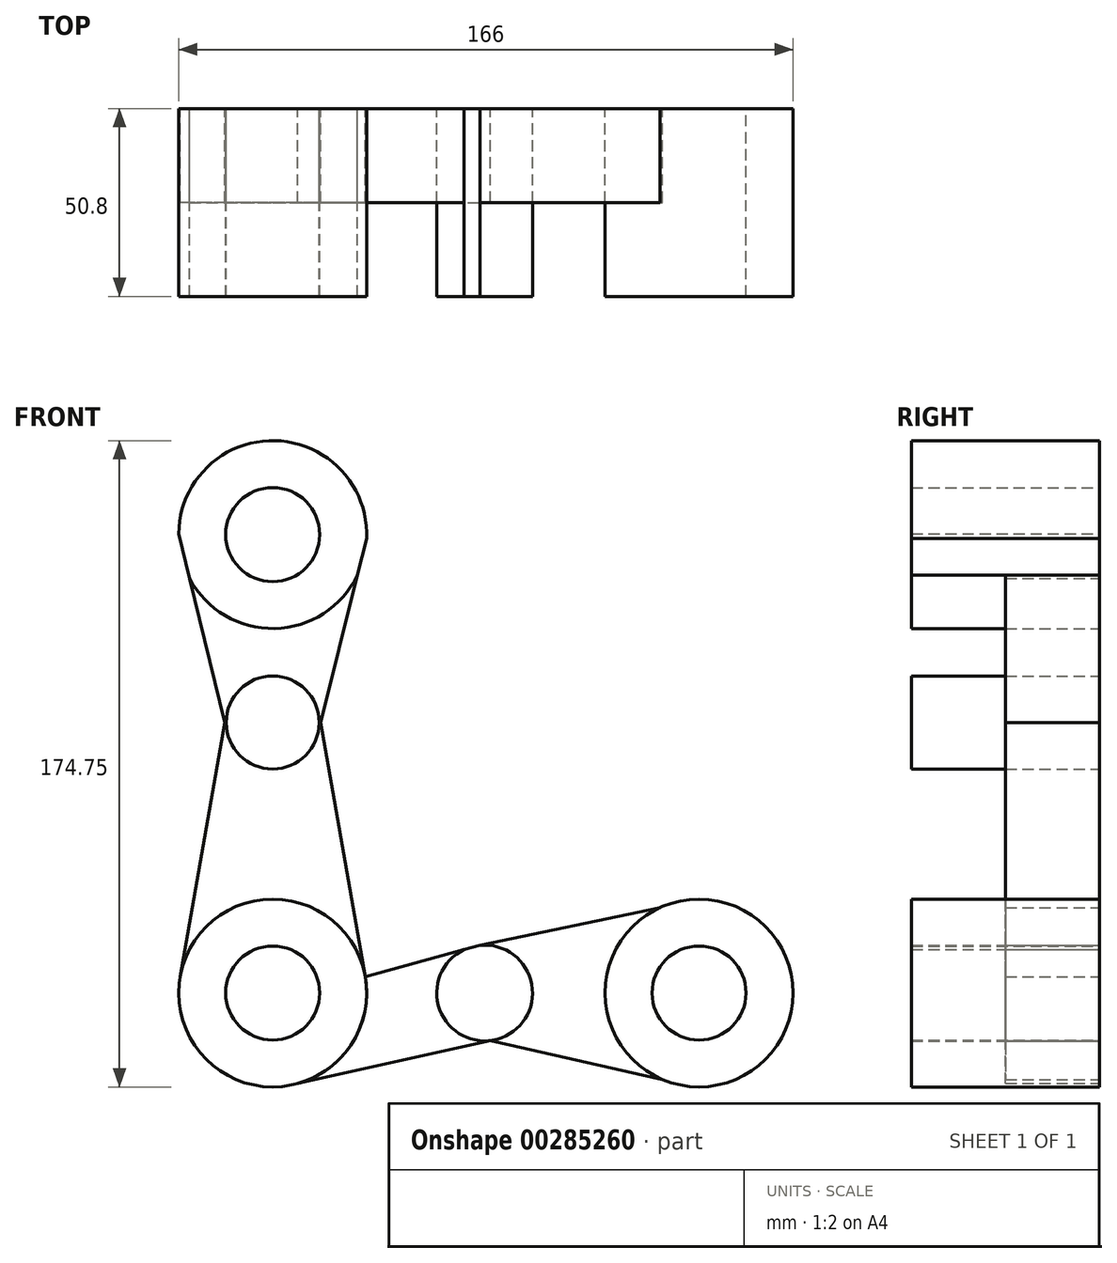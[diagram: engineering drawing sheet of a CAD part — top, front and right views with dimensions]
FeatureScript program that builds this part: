
annotation { "Feature Type Name" : "Feature", "Feature Type Description" : "" }
export const myFeature = defineFeature(function(context is Context, id is Id, definition is map)
    precondition{}
    {
        {
            var Q0;
            Q0=qCreatedBy(makeId("Front.planeOp"),FACE);
            var sketch = newSketch(context, id + "F0", { "sketchPlane" : qUnion([Q0])});
            skLineSegment(sketch, "E0", {"start": v(-57.93, -73.15) * mm, "end": v(-115.2, -73.15) * mm});
            skLineSegment(sketch, "E1", {"start": v(-57.93, -73.15) * mm, "end": v(0, -73.15) * mm});
            skLineSegment(sketch, "E2", {"start": v(-115.2, -73.15) * mm, "end": v(-115.2, 0) * mm});
            skLineSegment(sketch, "E3", {"start": v(-115.2, 0) * mm, "end": v(-115.2, 50.8) * mm});
            skCircle(sketch, "E4", {"center": v(-115.2, 50.8) * mm, "radius": 25.4 * mm});
            skCircle(sketch, "E5", {"center": v(-115.2, -73.15) * mm, "radius": 25.4 * mm});
            skCircle(sketch, "E6", {"center": v(0, -73.15) * mm, "radius": 25.4 * mm});
            skCircle(sketch, "E7", {"center": v(-115.2, 0) * mm, "radius": 12.57 * mm});
            skCircle(sketch, "E8", {"center": v(-57.93, -73.15) * mm, "radius": 12.95 * mm});
            skLineSegment(sketch, "E9", {"start": v(-140.6, 51.02) * mm, "end": v(-128.13, 0) * mm});
            skLineSegment(sketch, "E10", {"start": v(-128.13, 0) * mm, "end": v(-140.21, -68.75) * mm});
            skLineSegment(sketch, "E11", {"start": v(-89.82, 49.72) * mm, "end": v(-102.24, 0) * mm});
            skLineSegment(sketch, "E12", {"start": v(-102.24, 0) * mm, "end": v(-90.18, -68.75) * mm});
            skLineSegment(sketch, "E13", {"start": v(-90.18, -68.75) * mm, "end": v(-59.14, -60.25) * mm});
            skLineSegment(sketch, "E14", {"start": v(-59.14, -60.25) * mm, "end": v(-10.54, -50.04) * mm});
            skLineSegment(sketch, "E15", {"start": v(-56.39, -86) * mm, "end": v(-9.9, -96.54) * mm});
            skLineSegment(sketch, "E16", {"start": v(-108.46, -97.64) * mm, "end": v(-56.39, -86) * mm});
            skSolve(sketch);
        }
        {
            var Q0;
            {var subQ1=sQuery(id+"F0.wireOp",EDGE,"E4");var subQ6=makeQuery(id+"F0.imprint","INTERSECT",VERTEX,{"derivedFrom":[sQuery(id+"F0.wireOp",EDGE,"E3"),subQ1]});Q0=makeQuery(id+"F0.imprint","IMPRINT",FACE,{"disambiguationData":[TD([[makeQuery(id+"F0.imprint","IMPRINT",EDGE,{"disambiguationData":[TD([[subQ6,1.0]])],"derivedFrom":subQ1}),1.0]])]});}
            var Q1;
            {var subQ0=sQuery(id+"F0.wireOp",EDGE,"E3");var subQ1=sQuery(id+"F0.wireOp",EDGE,"E2");var subQ2=makeQuery(id+"F0.imprint","INTERSECT",VERTEX,{"derivedFrom":[subQ1,subQ0]});Q1=makeQuery(id+"F0.imprint","IMPRINT",FACE,{"disambiguationData":[TD([[makeQuery(id+"F0.imprint","IMPRINT",EDGE,{"disambiguationData":[TD([[subQ2,1.0]])],"derivedFrom":subQ1}),1.0]])]});}
            var Q2;
            {var subQ0=sQuery(id+"F0.wireOp",EDGE,"E3");var subQ1=sQuery(id+"F0.wireOp",EDGE,"E2");var subQ2=makeQuery(id+"F0.imprint","INTERSECT",VERTEX,{"derivedFrom":[subQ1,subQ0]});Q2=makeQuery(id+"F0.imprint","IMPRINT",FACE,{"disambiguationData":[TD([[makeQuery(id+"F0.imprint","IMPRINT",EDGE,{"disambiguationData":[TD([[subQ2,1.0]])],"derivedFrom":subQ1}),-1.0]])]});}
            var Q3;
            {var subQ3=sQuery(id+"F0.wireOp",EDGE,"E2");var subQ4=sQuery(id+"F0.wireOp",EDGE,"E0");var subQ5=makeQuery(id+"F0.imprint","INTERSECT",VERTEX,{"derivedFrom":[subQ4,subQ3]});Q3=makeQuery(id+"F0.imprint","IMPRINT",FACE,{"disambiguationData":[TD([[makeQuery(id+"F0.imprint","IMPRINT",EDGE,{"disambiguationData":[TD([[subQ5,1.0]])],"derivedFrom":subQ4}),1.0]])]});}
            var Q4;
            {var subQ0=sQuery(id+"F0.wireOp",EDGE,"E2");var subQ1=sQuery(id+"F0.wireOp",EDGE,"E0");var subQ2=makeQuery(id+"F0.imprint","INTERSECT",VERTEX,{"derivedFrom":[subQ1,subQ0]});Q4=makeQuery(id+"F0.imprint","IMPRINT",FACE,{"disambiguationData":[TD([[makeQuery(id+"F0.imprint","IMPRINT",EDGE,{"disambiguationData":[TD([[subQ2,1.0]])],"derivedFrom":subQ1}),-1.0]])]});}
            var Q5;
            {var subQ3=sQuery(id+"F0.wireOp",EDGE,"E0");var subQ5=sQuery(id+"F0.wireOp",EDGE,"E1");var subQ6=makeQuery(id+"F0.imprint","INTERSECT",VERTEX,{"derivedFrom":[subQ3,subQ5]});Q5=makeQuery(id+"F0.imprint","IMPRINT",FACE,{"disambiguationData":[TD([[makeQuery(id+"F0.imprint","IMPRINT",EDGE,{"disambiguationData":[TD([[subQ6,-1.0]])],"derivedFrom":subQ3}),-1.0]])]});}
            var Q6;
            {var subQ0=sQuery(id+"F0.wireOp",EDGE,"E1");var subQ1=sQuery(id+"F0.wireOp",EDGE,"E0");var subQ2=makeQuery(id+"F0.imprint","INTERSECT",VERTEX,{"derivedFrom":[subQ1,subQ0]});Q6=makeQuery(id+"F0.imprint","IMPRINT",FACE,{"disambiguationData":[TD([[makeQuery(id+"F0.imprint","IMPRINT",EDGE,{"disambiguationData":[TD([[subQ2,-1.0]])],"derivedFrom":subQ1}),1.0]])]});}
            var Q7;
            {var subQ0=sQuery(id+"F0.wireOp",EDGE,"E6");var subQ1=makeQuery(id+"F0.imprint","INTERSECT",VERTEX,{"derivedFrom":[subQ0,sQuery(id+"F0.wireOp",EDGE,"E14")]});Q7=makeQuery(id+"F0.imprint","IMPRINT",FACE,{"disambiguationData":[TD([[makeQuery(id+"F0.imprint","IMPRINT",EDGE,{"disambiguationData":[TD([[subQ1,-1.0]])],"derivedFrom":subQ0}),1.0]])]});}
            extrude(context, id + "F1", {"entities" : qUnion([Q0, Q1, Q2, Q3, Q4, Q5, Q6, Q7]), "depth" : 50.8 * mm});
        }
        {
            var Q0;
            {var subQ0=sQuery(id+"F0.wireOp",EDGE,"E10");Q0=makeQuery(id+"F0.imprint","IMPRINT",FACE,{"disambiguationData":[TD([[makeQuery(id+"F0.imprint","IMPRINT",EDGE,{"derivedFrom":subQ0}),1.0]])]});}
            var Q1;
            {var subQ5=sQuery(id+"F0.wireOp",EDGE,"E12");Q1=makeQuery(id+"F0.imprint","IMPRINT",FACE,{"disambiguationData":[TD([[makeQuery(id+"F0.imprint","IMPRINT",EDGE,{"derivedFrom":subQ5}),-1.0]])]});}
            var Q2;
            {var subQ0=sQuery(id+"F0.wireOp",EDGE,"E8");var subQ1=sQuery(id+"F0.wireOp",EDGE,"E0");var subQ2=makeQuery(id+"F0.imprint","INTERSECT",VERTEX,{"derivedFrom":[subQ1,subQ0]});Q2=makeQuery(id+"F0.imprint","IMPRINT",FACE,{"disambiguationData":[TD([[makeQuery(id+"F0.imprint","IMPRINT",EDGE,{"disambiguationData":[TD([[subQ2,-1.0]])],"derivedFrom":subQ1}),-1.0]])]});}
            var Q3;
            {var subQ5=sQuery(id+"F0.wireOp",EDGE,"E16");Q3=makeQuery(id+"F0.imprint","IMPRINT",FACE,{"disambiguationData":[TD([[makeQuery(id+"F0.imprint","IMPRINT",EDGE,{"derivedFrom":subQ5}),1.0]])]});}
            var Q4;
            {var subQ5=sQuery(id+"F0.wireOp",EDGE,"E14");Q4=makeQuery(id+"F0.imprint","IMPRINT",FACE,{"disambiguationData":[TD([[makeQuery(id+"F0.imprint","IMPRINT",EDGE,{"derivedFrom":subQ5}),-1.0]])]});}
            var Q5;
            {var subQ5=sQuery(id+"F0.wireOp",EDGE,"E15");Q5=makeQuery(id+"F0.imprint","IMPRINT",FACE,{"disambiguationData":[TD([[makeQuery(id+"F0.imprint","IMPRINT",EDGE,{"derivedFrom":subQ5}),1.0]])]});}
            extrude(context, id + "F2", {"entities" : qUnion([Q0, Q1, Q2, Q3, Q4, Q5]), "depth" : 25.4 * mm});
        }
        {
            var Q0;
            Q0=sQuery(id+"F0.wireOp",VERTEX,"E3.end");
            var Q1;
            Q1=sQuery(id+"F0.wireOp",VERTEX,"E5.center");
            var Q2;
            Q2=sQuery(id+"F0.wireOp",VERTEX,"E1.end");
            var Q3;
            Q3=makeQuery(id+"F1.opExtrude","SWEPT_BODY",BODY,{"disambiguationData":[OSD([sQuery(id+"F0.wireOp",EDGE,"E4"),sQuery(id+"F0.wireOp",EDGE,"E9"),sQuery(id+"F0.wireOp",EDGE,"E11")])]});
            var Q4;
            Q4=makeQuery(id+"F1.opExtrude","SWEPT_BODY",BODY,{"disambiguationData":[OSD([sQuery(id+"F0.wireOp",EDGE,"E5")])]});
            var Q5;
            Q5=makeQuery(id+"F1.opExtrude","SWEPT_BODY",BODY,{"disambiguationData":[OSD([sQuery(id+"F0.wireOp",EDGE,"E6")])]});
            hole(context, id + "F3", {"style" : HoleStyle.SIMPLE, "endStyle" : HoleEndStyle.THROUGH, "oppositeDirection" : true, "holeDiameter" : 25.4 * mm, "isTappedThrough" : true, "tappedDepth" : 12.7 * mm, "tapClearance" : 3, "locations" : qUnion([Q0, Q1, Q2]), "scope" : qUnion([Q3, Q4, Q5])});
        }
    });
